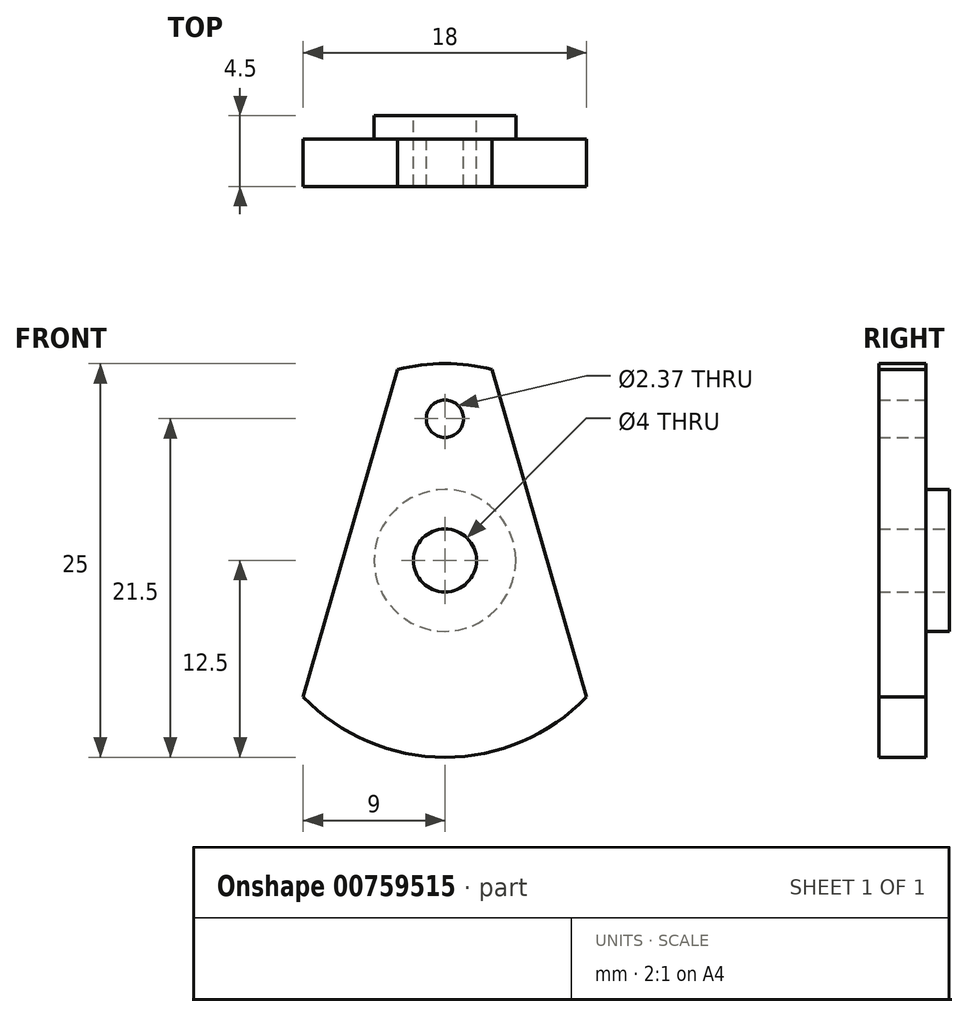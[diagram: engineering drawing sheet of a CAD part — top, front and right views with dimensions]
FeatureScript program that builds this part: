
annotation { "Feature Type Name" : "Feature", "Feature Type Description" : "" }
export const myFeature = defineFeature(function(context is Context, id is Id, definition is map)
    precondition{}
    {
        {
            var Q0;
            Q0=qCreatedBy(makeId("Front.planeOp"),FACE);
            var sketch = newSketch(context, id + "F0", { "sketchPlane" : qUnion([Q0])});
            skCircle(sketch, "E0", {"center": v(0, 0) * mm, "radius": 4.5 * mm});
            skCircle(sketch, "E1", {"center": v(0, 0) * mm, "radius": 2 * mm});
            skArc(sketch, "E2", {"start": v(3, 12.13) * mm, "mid": v(0, 12.5) * mm, "end": v(-3, 12.13) * mm});
            skLineSegment(sketch, "E3", {"start": v(9, -8.67) * mm, "end": v(3, 12.13) * mm});
            skLineSegment(sketch, "E4.MirrorCS", {"start": v(-9, -8.67) * mm, "end": v(-3, 12.13) * mm});
            skArc(sketch, "E5.trimOffspring", {"start": v(-9, -8.67) * mm, "mid": v(0, -12.5) * mm, "end": v(9, -8.67) * mm});
            skCircle(sketch, "E6", {"center": v(0, 9) * mm, "radius": 1.19 * mm});
            skSolve(sketch);
        }
        {
            var Q0;
            Q0 = qSketchRegion(id + "F0", true);
            var Q1;
            Q1=makeQuery(id+"F0.imprint","IMPRINT",FACE,{"disambiguationData":[TD([[makeQuery(id+"F0.imprint","IMPRINT",EDGE,{"derivedFrom":sQuery(id+"F0.wireOp",EDGE,"E0")}),1.0]])]});
            extrude(context, id + "F1", {"entities" : qUnion([Q0, Q1]), "depth" : 3 * mm, "offsetDistance" : 25 * mm});
        }
        {
            var Q0;
            Q0=makeQuery(id+"F0.imprint","IMPRINT",FACE,{"disambiguationData":[TD([[makeQuery(id+"F0.imprint","IMPRINT",EDGE,{"derivedFrom":sQuery(id+"F0.wireOp",EDGE,"E0")}),1.0]])]});
            extrude(context, id + "F2", {"entities" : qUnion([Q0]), "operationType" : NewBodyOperationType.ADD, "oppositeDirection" : true, "depth" : 1.5 * mm, "offsetDistance" : 25 * mm});
        }
    });
